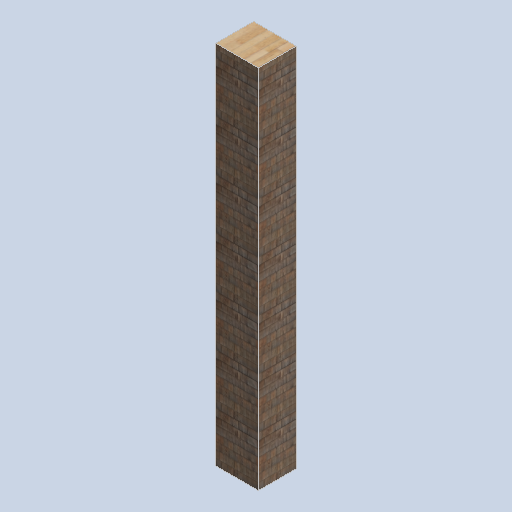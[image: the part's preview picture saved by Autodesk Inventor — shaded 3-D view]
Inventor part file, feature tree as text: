
AUTODESK INVENTOR PART (.ipt)
format: ipt  version: 2024.2 (Build 282272000, 272)  size: 164,352 bytes
history: native  units: in
note: dims shown in document units (in); Inventor stores cm internally (conversion verified against a paired STEP export)
features: other x3, sketch x1
ambient origin geometry x8: Origin, YZ Plane, XZ Plane, XY Plane, X Axis, Y Axis, Z Axis, Center Point
bodies: Solid1 (feature_tree)
feature tree (4):
  other  "support_column_01_MIR.ipt"
  other  "Solid1::support_column_01_MIR.ipt"
  other  "TaggingFeature1"
  sketch  "Sketch1"  dims[d0=0.3937in]
